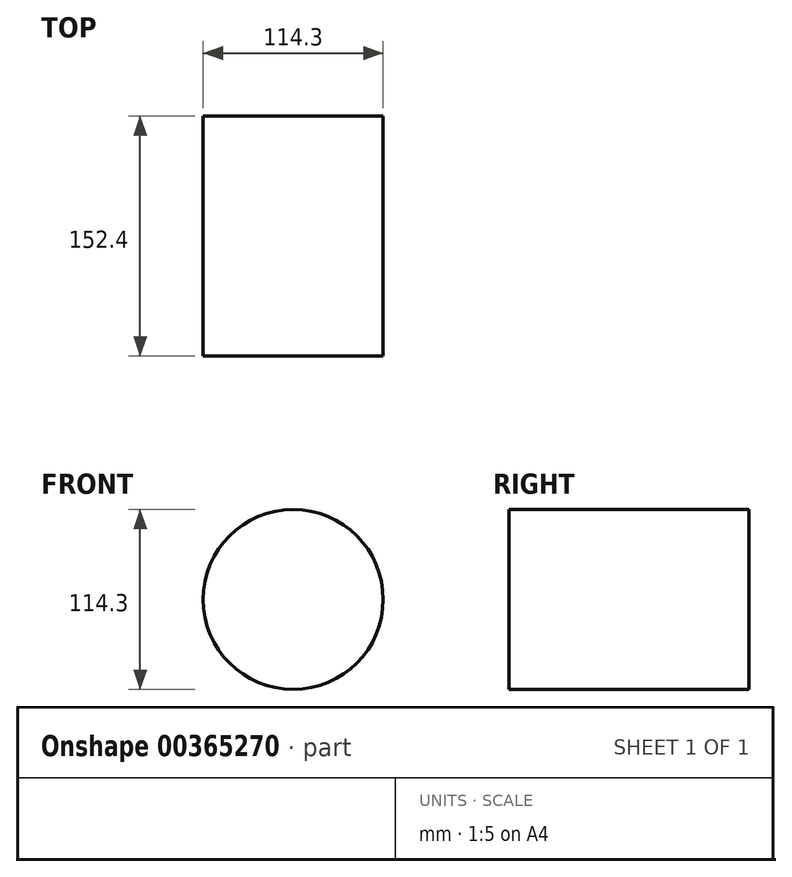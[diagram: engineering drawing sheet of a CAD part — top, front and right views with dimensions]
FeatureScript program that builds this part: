
annotation { "Feature Type Name" : "Feature", "Feature Type Description" : "" }
export const myFeature = defineFeature(function(context is Context, id is Id, definition is map)
    precondition{}
    {
        {
            var Q0;
            Q0=qCreatedBy(makeId("Front.planeOp"),FACE);
            var sketch = newSketch(context, id + "F0", { "sketchPlane" : qUnion([Q0])});
            skCircle(sketch, "E0", {"center": v(-21.98, -12.42) * mm, "radius": 57.15 * mm});
            skSolve(sketch);
        }
        {
            var Q0;
            Q0=qSketchRegion(id+"F0",true);
            extrude(context, id + "F1", {"entities" : qUnion([Q0]), "depth" : 152.4 * mm});
        }
    });
